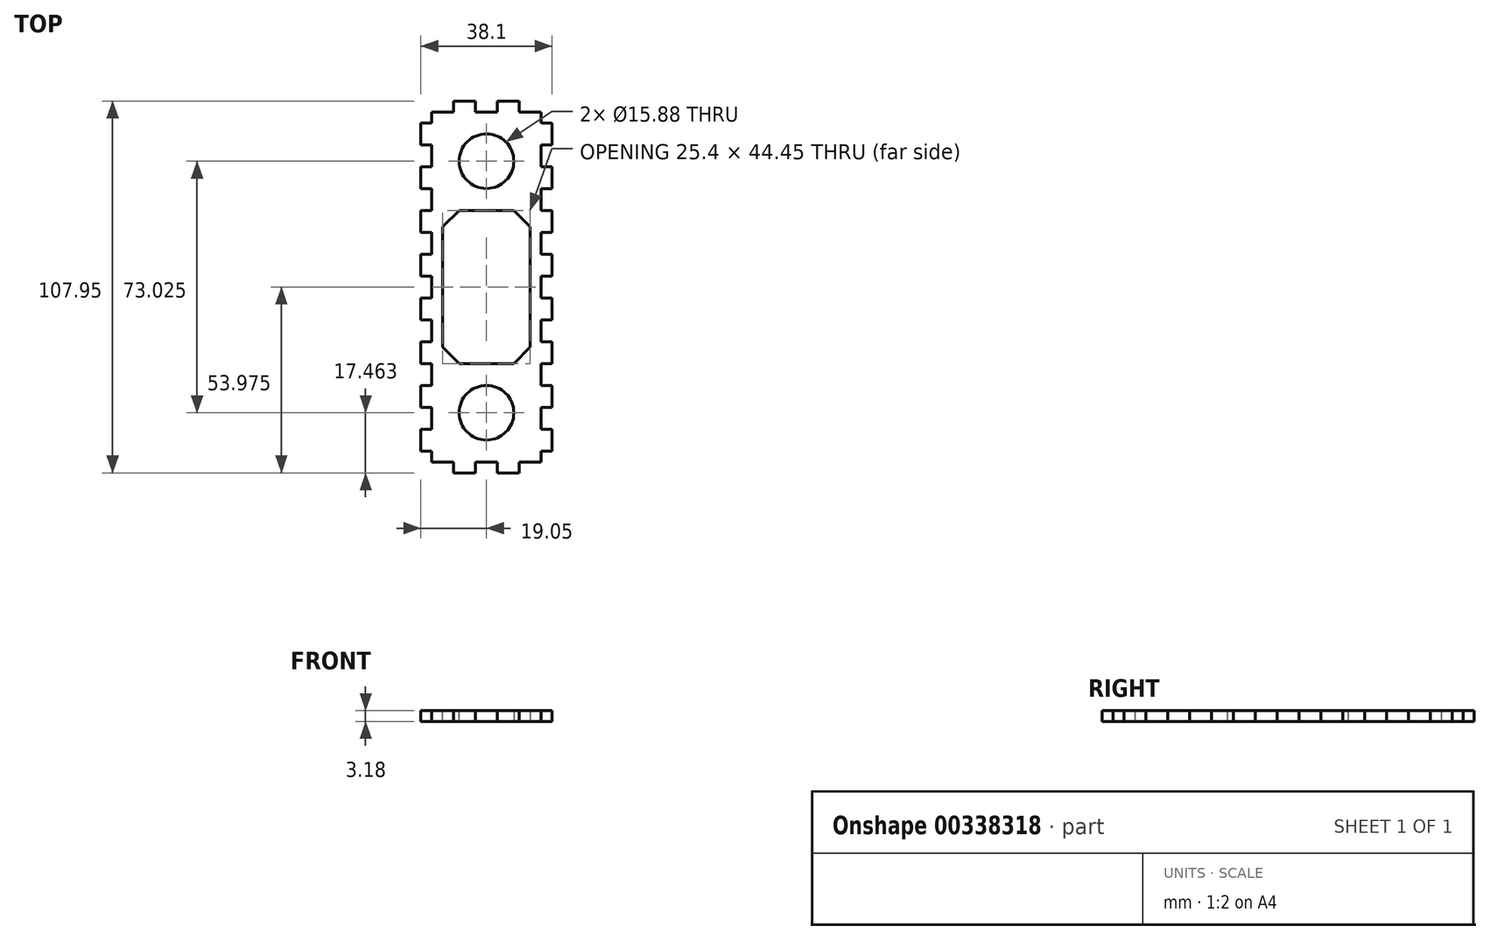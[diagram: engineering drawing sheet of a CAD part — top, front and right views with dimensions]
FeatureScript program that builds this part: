
annotation { "Feature Type Name" : "Feature", "Feature Type Description" : "" }
export const myFeature = defineFeature(function(context is Context, id is Id, definition is map)
    precondition{}
    {
        {
            var Q0;
            Q0=qCreatedBy(makeId("Top.planeOp"),FACE);
            var sketch = newSketch(context, id + "F0", { "sketchPlane" : qUnion([Q0])});
            skLineSegment(sketch, "E0.bottom", {"start": v(0, 0) * mm, "end": v(38.1, 0) * mm});
            skLineSegment(sketch, "E0.top", {"start": v(0, -107.95) * mm, "end": v(38.1, -107.95) * mm});
            skLineSegment(sketch, "E0.left", {"start": v(0, 0) * mm, "end": v(0, -107.95) * mm});
            skLineSegment(sketch, "E0.right", {"start": v(38.1, 0) * mm, "end": v(38.1, -107.95) * mm});
            skLineSegment(sketch, "E1", {"start": v(19.05, 0) * mm, "end": v(19.05, -17.46) * mm, "construction": true});
            skCircle(sketch, "E2", {"center": v(19.05, -17.46) * mm, "radius": 7.94 * mm});
            skLineSegment(sketch, "E3", {"start": v(19.05, -17.46) * mm, "end": v(19.05, -90.49) * mm, "construction": true});
            skLineSegment(sketch, "E4", {"start": v(19.05, -90.49) * mm, "end": v(19.05, -107.95) * mm, "construction": true});
            skCircle(sketch, "E5", {"center": v(19.05, -90.49) * mm, "radius": 7.94 * mm});
            skSolve(sketch);
        }
        {
            var Q0;
            Q0=qSketchRegion(id+"F0",true);
            extrude(context, id + "F1", {"entities" : qUnion([Q0]), "depth" : 3.17 * mm});
        }
        {
            var Q0;
            Q0=makeQuery(id+"F1.opExtrude","CAP_FACE",FACE,{"disambiguationData":[OSD([sQuery(id+"F0.wireOp",EDGE,"E0.bottom"),sQuery(id+"F0.wireOp",EDGE,"E0.top"),sQuery(id+"F0.wireOp",EDGE,"E0.left"),sQuery(id+"F0.wireOp",EDGE,"E0.right"),sQuery(id+"F0.wireOp",EDGE,"E2"),sQuery(id+"F0.wireOp",EDGE,"E5")])],"isStart":false});
            var sketch = newSketch(context, id + "F2", { "sketchPlane" : qUnion([Q0])});
            skLineSegment(sketch, "E6.bottom", {"start": v(38.1, 0) * mm, "end": v(34.93, 0) * mm});
            skLineSegment(sketch, "E6.top", {"start": v(38.1, -6.35) * mm, "end": v(34.93, -6.35) * mm});
            skLineSegment(sketch, "E6.left", {"start": v(38.1, 0) * mm, "end": v(38.1, -6.35) * mm});
            skLineSegment(sketch, "E6.right", {"start": v(34.93, 0) * mm, "end": v(34.93, -6.35) * mm});
            skLineSegment(sketch, "E7.bottom", {"start": v(0, 0) * mm, "end": v(3.17, 0) * mm});
            skLineSegment(sketch, "E7.top", {"start": v(0, -6.35) * mm, "end": v(3.17, -6.35) * mm});
            skLineSegment(sketch, "E7.left", {"start": v(0, 0) * mm, "end": v(0, -6.35) * mm});
            skLineSegment(sketch, "E7.right", {"start": v(3.17, 0) * mm, "end": v(3.17, -6.35) * mm});
            skLineSegment(sketch, "E8", {"start": v(3.17, -6.35) * mm, "end": v(3.17, -12.7) * mm, "construction": true});
            skLineSegment(sketch, "E9.bottom", {"start": v(3.17, -12.7) * mm, "end": v(0, -12.7) * mm});
            skLineSegment(sketch, "E9.top", {"start": v(3.17, -19.05) * mm, "end": v(0, -19.05) * mm});
            skLineSegment(sketch, "E9.left", {"start": v(3.17, -12.7) * mm, "end": v(3.17, -19.05) * mm});
            skLineSegment(sketch, "E9.right", {"start": v(0, -12.7) * mm, "end": v(0, -19.05) * mm});
            skLineSegment(sketch, "E10", {"start": v(34.93, -6.35) * mm, "end": v(34.93, -12.7) * mm, "construction": true});
            skLineSegment(sketch, "E11.bottom", {"start": v(34.93, -12.7) * mm, "end": v(38.1, -12.7) * mm});
            skLineSegment(sketch, "E11.top", {"start": v(34.93, -19.05) * mm, "end": v(38.1, -19.05) * mm});
            skLineSegment(sketch, "E11.left", {"start": v(34.93, -12.7) * mm, "end": v(34.93, -19.05) * mm});
            skLineSegment(sketch, "E11.right", {"start": v(38.1, -12.7) * mm, "end": v(38.1, -19.05) * mm});
            skLineSegment(sketch, "E12.0.1.0", {"start": v(34.93, -25.4) * mm, "end": v(38.1, -25.4) * mm});
            skLineSegment(sketch, "E12.0.1.1", {"start": v(34.93, -31.75) * mm, "end": v(38.1, -31.75) * mm});
            skLineSegment(sketch, "E12.0.1.2", {"start": v(34.93, -19.05) * mm, "end": v(34.93, -25.4) * mm, "construction": true});
            skLineSegment(sketch, "E12.0.1.3", {"start": v(38.1, -25.4) * mm, "end": v(38.1, -31.75) * mm});
            skLineSegment(sketch, "E12.0.1.4", {"start": v(34.93, -25.4) * mm, "end": v(34.93, -31.75) * mm});
            skLineSegment(sketch, "E12.0.2.0", {"start": v(34.93, -38.1) * mm, "end": v(38.1, -38.1) * mm});
            skLineSegment(sketch, "E12.0.2.1", {"start": v(34.93, -44.45) * mm, "end": v(38.1, -44.45) * mm});
            skLineSegment(sketch, "E12.0.2.2", {"start": v(34.93, -31.75) * mm, "end": v(34.93, -38.1) * mm, "construction": true});
            skLineSegment(sketch, "E12.0.2.3", {"start": v(38.1, -38.1) * mm, "end": v(38.1, -44.45) * mm});
            skLineSegment(sketch, "E12.0.2.4", {"start": v(34.93, -38.1) * mm, "end": v(34.93, -44.45) * mm});
            skLineSegment(sketch, "E12.0.3.0", {"start": v(34.93, -50.8) * mm, "end": v(38.1, -50.8) * mm});
            skLineSegment(sketch, "E12.0.3.1", {"start": v(34.93, -57.15) * mm, "end": v(38.1, -57.15) * mm});
            skLineSegment(sketch, "E12.0.3.2", {"start": v(34.93, -44.45) * mm, "end": v(34.93, -50.8) * mm, "construction": true});
            skLineSegment(sketch, "E12.0.3.3", {"start": v(38.1, -50.8) * mm, "end": v(38.1, -57.15) * mm});
            skLineSegment(sketch, "E12.0.3.4", {"start": v(34.93, -50.8) * mm, "end": v(34.93, -57.15) * mm});
            skLineSegment(sketch, "E12.0.4.0", {"start": v(34.93, -63.5) * mm, "end": v(38.1, -63.5) * mm});
            skLineSegment(sketch, "E12.0.4.1", {"start": v(34.93, -69.85) * mm, "end": v(38.1, -69.85) * mm});
            skLineSegment(sketch, "E12.0.4.2", {"start": v(34.93, -57.15) * mm, "end": v(34.93, -63.5) * mm, "construction": true});
            skLineSegment(sketch, "E12.0.4.3", {"start": v(38.1, -63.5) * mm, "end": v(38.1, -69.85) * mm});
            skLineSegment(sketch, "E12.0.4.4", {"start": v(34.93, -63.5) * mm, "end": v(34.93, -69.85) * mm});
            skLineSegment(sketch, "E12.0.5.0", {"start": v(34.93, -76.2) * mm, "end": v(38.1, -76.2) * mm});
            skLineSegment(sketch, "E12.0.5.1", {"start": v(34.93, -82.55) * mm, "end": v(38.1, -82.55) * mm});
            skLineSegment(sketch, "E12.0.5.2", {"start": v(34.93, -69.85) * mm, "end": v(34.93, -76.2) * mm, "construction": true});
            skLineSegment(sketch, "E12.0.5.3", {"start": v(38.1, -76.2) * mm, "end": v(38.1, -82.55) * mm});
            skLineSegment(sketch, "E12.0.5.4", {"start": v(34.93, -76.2) * mm, "end": v(34.93, -82.55) * mm});
            skLineSegment(sketch, "E12.0.6.0", {"start": v(34.93, -88.9) * mm, "end": v(38.1, -88.9) * mm});
            skLineSegment(sketch, "E12.0.6.1", {"start": v(34.93, -95.25) * mm, "end": v(38.1, -95.25) * mm});
            skLineSegment(sketch, "E12.0.6.2", {"start": v(34.93, -82.55) * mm, "end": v(34.93, -88.9) * mm, "construction": true});
            skLineSegment(sketch, "E12.0.6.3", {"start": v(38.1, -88.9) * mm, "end": v(38.1, -95.25) * mm});
            skLineSegment(sketch, "E12.0.6.4", {"start": v(34.93, -88.9) * mm, "end": v(34.93, -95.25) * mm});
            skLineSegment(sketch, "E12.0.7.0", {"start": v(34.93, -101.6) * mm, "end": v(38.1, -101.6) * mm});
            skLineSegment(sketch, "E12.0.7.1", {"start": v(34.93, -107.95) * mm, "end": v(38.1, -107.95) * mm});
            skLineSegment(sketch, "E12.0.7.2", {"start": v(34.93, -95.25) * mm, "end": v(34.93, -101.6) * mm, "construction": true});
            skLineSegment(sketch, "E12.0.7.3", {"start": v(38.1, -101.6) * mm, "end": v(38.1, -107.95) * mm});
            skLineSegment(sketch, "E12.0.7.4", {"start": v(34.93, -101.6) * mm, "end": v(34.93, -107.95) * mm});
            skLineSegment(sketch, "E12.0.8.0", {"start": v(34.93, -114.3) * mm, "end": v(38.1, -114.3) * mm});
            skLineSegment(sketch, "E12.0.8.1", {"start": v(34.93, -120.65) * mm, "end": v(38.1, -120.65) * mm});
            skLineSegment(sketch, "E12.0.8.2", {"start": v(34.93, -107.95) * mm, "end": v(34.93, -114.3) * mm, "construction": true});
            skLineSegment(sketch, "E12.0.8.3", {"start": v(38.1, -114.3) * mm, "end": v(38.1, -120.65) * mm});
            skLineSegment(sketch, "E12.0.8.4", {"start": v(34.93, -114.3) * mm, "end": v(34.93, -120.65) * mm});
            skLineSegment(sketch, "E12.0.9.0", {"start": v(34.93, -127) * mm, "end": v(38.1, -127) * mm});
            skLineSegment(sketch, "E12.0.9.1", {"start": v(34.93, -133.35) * mm, "end": v(38.1, -133.35) * mm});
            skLineSegment(sketch, "E12.0.9.2", {"start": v(34.93, -120.65) * mm, "end": v(34.93, -127) * mm, "construction": true});
            skLineSegment(sketch, "E12.0.9.3", {"start": v(38.1, -127) * mm, "end": v(38.1, -133.35) * mm});
            skLineSegment(sketch, "E12.0.9.4", {"start": v(34.93, -127) * mm, "end": v(34.93, -133.35) * mm});
            skLineSegment(sketch, "E12.direction1", {"start": v(17.46, -19.05) * mm, "end": v(34.93, -19.05) * mm, "construction": true});
            skLineSegment(sketch, "E12.direction2", {"start": v(34.93, -19.05) * mm, "end": v(34.93, -31.75) * mm, "construction": true});
            skLineSegment(sketch, "E13.0.1.0", {"start": v(3.17, -19.05) * mm, "end": v(3.17, -25.4) * mm, "construction": true});
            skLineSegment(sketch, "E13.0.1.1", {"start": v(3.17, -25.4) * mm, "end": v(0, -25.4) * mm});
            skLineSegment(sketch, "E13.0.1.2", {"start": v(3.17, -31.75) * mm, "end": v(0, -31.75) * mm});
            skLineSegment(sketch, "E13.0.1.3", {"start": v(3.17, -25.4) * mm, "end": v(3.17, -31.75) * mm});
            skLineSegment(sketch, "E13.0.1.4", {"start": v(0, -25.4) * mm, "end": v(0, -31.75) * mm});
            skLineSegment(sketch, "E13.0.2.0", {"start": v(3.17, -31.75) * mm, "end": v(3.17, -38.1) * mm, "construction": true});
            skLineSegment(sketch, "E13.0.2.1", {"start": v(3.17, -38.1) * mm, "end": v(0, -38.1) * mm});
            skLineSegment(sketch, "E13.0.2.2", {"start": v(3.17, -44.45) * mm, "end": v(0, -44.45) * mm});
            skLineSegment(sketch, "E13.0.2.3", {"start": v(3.17, -38.1) * mm, "end": v(3.17, -44.45) * mm});
            skLineSegment(sketch, "E13.0.2.4", {"start": v(0, -38.1) * mm, "end": v(0, -44.45) * mm});
            skLineSegment(sketch, "E13.0.3.0", {"start": v(3.17, -44.45) * mm, "end": v(3.17, -50.8) * mm, "construction": true});
            skLineSegment(sketch, "E13.0.3.1", {"start": v(3.17, -50.8) * mm, "end": v(0, -50.8) * mm});
            skLineSegment(sketch, "E13.0.3.2", {"start": v(3.17, -57.15) * mm, "end": v(0, -57.15) * mm});
            skLineSegment(sketch, "E13.0.3.3", {"start": v(3.17, -50.8) * mm, "end": v(3.17, -57.15) * mm});
            skLineSegment(sketch, "E13.0.3.4", {"start": v(0, -50.8) * mm, "end": v(0, -57.15) * mm});
            skLineSegment(sketch, "E13.0.4.0", {"start": v(3.17, -57.15) * mm, "end": v(3.17, -63.5) * mm, "construction": true});
            skLineSegment(sketch, "E13.0.4.1", {"start": v(3.17, -63.5) * mm, "end": v(0, -63.5) * mm});
            skLineSegment(sketch, "E13.0.4.2", {"start": v(3.17, -69.85) * mm, "end": v(0, -69.85) * mm});
            skLineSegment(sketch, "E13.0.4.3", {"start": v(3.17, -63.5) * mm, "end": v(3.17, -69.85) * mm});
            skLineSegment(sketch, "E13.0.4.4", {"start": v(0, -63.5) * mm, "end": v(0, -69.85) * mm});
            skLineSegment(sketch, "E13.0.5.0", {"start": v(3.17, -69.85) * mm, "end": v(3.17, -76.2) * mm, "construction": true});
            skLineSegment(sketch, "E13.0.5.1", {"start": v(3.17, -76.2) * mm, "end": v(0, -76.2) * mm});
            skLineSegment(sketch, "E13.0.5.2", {"start": v(3.17, -82.55) * mm, "end": v(0, -82.55) * mm});
            skLineSegment(sketch, "E13.0.5.3", {"start": v(3.17, -76.2) * mm, "end": v(3.17, -82.55) * mm});
            skLineSegment(sketch, "E13.0.5.4", {"start": v(0, -76.2) * mm, "end": v(0, -82.55) * mm});
            skLineSegment(sketch, "E13.0.6.0", {"start": v(3.17, -82.55) * mm, "end": v(3.17, -88.9) * mm, "construction": true});
            skLineSegment(sketch, "E13.0.6.1", {"start": v(3.17, -88.9) * mm, "end": v(0, -88.9) * mm});
            skLineSegment(sketch, "E13.0.6.2", {"start": v(3.17, -95.25) * mm, "end": v(0, -95.25) * mm});
            skLineSegment(sketch, "E13.0.6.3", {"start": v(3.17, -88.9) * mm, "end": v(3.17, -95.25) * mm});
            skLineSegment(sketch, "E13.0.6.4", {"start": v(0, -88.9) * mm, "end": v(0, -95.25) * mm});
            skLineSegment(sketch, "E13.0.7.0", {"start": v(3.17, -95.25) * mm, "end": v(3.17, -101.6) * mm, "construction": true});
            skLineSegment(sketch, "E13.0.7.1", {"start": v(3.17, -101.6) * mm, "end": v(0, -101.6) * mm});
            skLineSegment(sketch, "E13.0.7.2", {"start": v(3.17, -107.95) * mm, "end": v(0, -107.95) * mm});
            skLineSegment(sketch, "E13.0.7.3", {"start": v(3.17, -101.6) * mm, "end": v(3.17, -107.95) * mm});
            skLineSegment(sketch, "E13.0.7.4", {"start": v(0, -101.6) * mm, "end": v(0, -107.95) * mm});
            skLineSegment(sketch, "E13.0.8.0", {"start": v(3.17, -107.95) * mm, "end": v(3.17, -114.3) * mm, "construction": true});
            skLineSegment(sketch, "E13.0.8.1", {"start": v(3.17, -114.3) * mm, "end": v(0, -114.3) * mm});
            skLineSegment(sketch, "E13.0.8.2", {"start": v(3.17, -120.65) * mm, "end": v(0, -120.65) * mm});
            skLineSegment(sketch, "E13.0.8.3", {"start": v(3.17, -114.3) * mm, "end": v(3.17, -120.65) * mm});
            skLineSegment(sketch, "E13.0.8.4", {"start": v(0, -114.3) * mm, "end": v(0, -120.65) * mm});
            skLineSegment(sketch, "E13.0.9.0", {"start": v(3.17, -120.65) * mm, "end": v(3.17, -127) * mm, "construction": true});
            skLineSegment(sketch, "E13.0.9.1", {"start": v(3.17, -127) * mm, "end": v(0, -127) * mm});
            skLineSegment(sketch, "E13.0.9.2", {"start": v(3.17, -133.35) * mm, "end": v(0, -133.35) * mm});
            skLineSegment(sketch, "E13.0.9.3", {"start": v(3.17, -127) * mm, "end": v(3.17, -133.35) * mm});
            skLineSegment(sketch, "E13.0.9.4", {"start": v(0, -127) * mm, "end": v(0, -133.35) * mm});
            skLineSegment(sketch, "E13.direction1", {"start": v(0, -19.05) * mm, "end": v(17.46, -19.05) * mm, "construction": true});
            skLineSegment(sketch, "E13.direction2", {"start": v(0, -19.05) * mm, "end": v(0, -31.75) * mm, "construction": true});
            skLineSegment(sketch, "E14", {"start": v(19.05, 0) * mm, "end": v(19.05, -17.46) * mm, "construction": true});
            skLineSegment(sketch, "E15", {"start": v(19.05, -17.46) * mm, "end": v(19.05, -31.75) * mm, "construction": true});
            skLineSegment(sketch, "E16.bottom", {"start": v(6.35, -31.75) * mm, "end": v(31.75, -31.75) * mm});
            skLineSegment(sketch, "E16.top", {"start": v(6.35, -76.2) * mm, "end": v(31.75, -76.2) * mm});
            skLineSegment(sketch, "E16.left", {"start": v(6.35, -31.75) * mm, "end": v(6.35, -76.2) * mm});
            skLineSegment(sketch, "E16.right", {"start": v(31.75, -31.75) * mm, "end": v(31.75, -76.2) * mm});
            skLineSegment(sketch, "E17", {"start": v(31.75, -53.97) * mm, "end": v(34.93, -53.97) * mm, "construction": true});
            skPoint(sketch, "E18.oppositeSnap0", {"position": v(38.1, -3.18) * mm});
            skLineSegment(sketch, "E18.bottom", {"start": v(3.17, 0) * mm, "end": v(9.52, 0) * mm});
            skLineSegment(sketch, "E18.top", {"start": v(3.17, -3.17) * mm, "end": v(9.52, -3.17) * mm});
            skLineSegment(sketch, "E18.left", {"start": v(3.17, 0) * mm, "end": v(3.17, -3.18) * mm});
            skLineSegment(sketch, "E18.right", {"start": v(9.52, 0) * mm, "end": v(9.52, -3.18) * mm});
            skLineSegment(sketch, "E19.bottom", {"start": v(34.93, 0) * mm, "end": v(28.58, 0) * mm});
            skLineSegment(sketch, "E19.top", {"start": v(34.93, -3.17) * mm, "end": v(28.58, -3.17) * mm});
            skLineSegment(sketch, "E19.left", {"start": v(34.93, 0) * mm, "end": v(34.93, -3.18) * mm});
            skLineSegment(sketch, "E19.right", {"start": v(28.58, 0) * mm, "end": v(28.58, -3.18) * mm});
            skLineSegment(sketch, "E20.bottom", {"start": v(15.88, 0) * mm, "end": v(22.23, 0) * mm});
            skLineSegment(sketch, "E20.top", {"start": v(15.88, -3.17) * mm, "end": v(22.23, -3.17) * mm});
            skLineSegment(sketch, "E20.left", {"start": v(15.88, 0) * mm, "end": v(15.88, -3.18) * mm});
            skLineSegment(sketch, "E20.right", {"start": v(22.23, 0) * mm, "end": v(22.23, -3.18) * mm});
            skLineSegment(sketch, "E21", {"start": v(9.52, -3.18) * mm, "end": v(15.88, -3.17) * mm, "construction": true});
            skLineSegment(sketch, "E22", {"start": v(22.23, -3.17) * mm, "end": v(28.58, -3.17) * mm, "construction": true});
            skLineSegment(sketch, "E23", {"start": v(19.05, -90.49) * mm, "end": v(19.05, -107.95) * mm, "construction": true});
            skLineSegment(sketch, "E24.bottom", {"start": v(3.17, -107.95) * mm, "end": v(9.52, -107.95) * mm});
            skLineSegment(sketch, "E24.top", {"start": v(3.17, -104.78) * mm, "end": v(9.53, -104.78) * mm});
            skLineSegment(sketch, "E24.left", {"start": v(3.17, -107.95) * mm, "end": v(3.17, -104.78) * mm});
            skLineSegment(sketch, "E24.right", {"start": v(9.52, -107.95) * mm, "end": v(9.52, -104.78) * mm});
            skLineSegment(sketch, "E25.bottom", {"start": v(34.93, -107.95) * mm, "end": v(28.58, -107.95) * mm});
            skLineSegment(sketch, "E25.top", {"start": v(34.93, -104.78) * mm, "end": v(28.58, -104.78) * mm});
            skLineSegment(sketch, "E25.left", {"start": v(34.93, -107.95) * mm, "end": v(34.93, -104.78) * mm});
            skLineSegment(sketch, "E25.right", {"start": v(28.58, -107.95) * mm, "end": v(28.58, -104.78) * mm});
            skLineSegment(sketch, "E26.bottom", {"start": v(22.22, -107.95) * mm, "end": v(15.88, -107.95) * mm});
            skLineSegment(sketch, "E26.top", {"start": v(22.23, -104.78) * mm, "end": v(15.88, -104.78) * mm});
            skLineSegment(sketch, "E26.left", {"start": v(22.22, -107.95) * mm, "end": v(22.22, -104.78) * mm});
            skLineSegment(sketch, "E26.right", {"start": v(15.88, -107.95) * mm, "end": v(15.88, -104.78) * mm});
            skLineSegment(sketch, "E27", {"start": v(9.53, -104.78) * mm, "end": v(15.88, -104.78) * mm, "construction": true});
            skLineSegment(sketch, "E28", {"start": v(22.23, -104.78) * mm, "end": v(28.58, -104.78) * mm, "construction": true});
            skLineSegment(sketch, "E29", {"start": v(19.05, -90.49) * mm, "end": v(19.05, -76.2) * mm, "construction": true});
            skSolve(sketch);
        }
        {
            var Q0;
            Q0=qSketchRegion(id+"F2",true);
            var Q1;
            Q1=makeQuery(id+"F1.opExtrude","CAP_FACE",FACE,{"disambiguationData":[OSD([sQuery(id+"F0.wireOp",EDGE,"E0.bottom"),sQuery(id+"F0.wireOp",EDGE,"E0.top"),sQuery(id+"F0.wireOp",EDGE,"E0.left"),sQuery(id+"F0.wireOp",EDGE,"E0.right"),sQuery(id+"F0.wireOp",EDGE,"E2"),sQuery(id+"F0.wireOp",EDGE,"E5")])],"isStart":true});
            extrude(context, id + "F3", {"entities" : qUnion([Q0]), "operationType" : NewBodyOperationType.REMOVE, "endBound" : BoundingType.UP_TO_SURFACE, "oppositeDirection" : true, "endBoundEntityFace" : qUnion([Q1]), "depth" : 25.4 * mm});
        }
        {
            var Q0;
            Q0=makeQuery(id+"F3.boolean.opBoolean","COPY",EDGE,{"derivedFrom":makeQuery(id+"F3.opExtrude","SWEPT_EDGE",EDGE,{"disambiguationData":[OSD([sQuery(id+"F2.wireOp",EDGE,"E16.bottom"),sQuery(id+"F2.wireOp",EDGE,"E16.right")])]})});
            var Q1;
            Q1=makeQuery(id+"F3.boolean.opBoolean","COPY",EDGE,{"derivedFrom":makeQuery(id+"F3.opExtrude","SWEPT_EDGE",EDGE,{"disambiguationData":[OSD([sQuery(id+"F2.wireOp",EDGE,"E16.top"),sQuery(id+"F2.wireOp",EDGE,"E16.right")])]})});
            var Q2;
            Q2=makeQuery(id+"F3.boolean.opBoolean","COPY",EDGE,{"derivedFrom":makeQuery(id+"F3.opExtrude","SWEPT_EDGE",EDGE,{"disambiguationData":[OSD([sQuery(id+"F2.wireOp",EDGE,"E16.top"),sQuery(id+"F2.wireOp",EDGE,"E16.left")])]})});
            var Q3;
            Q3=makeQuery(id+"F3.boolean.opBoolean","COPY",EDGE,{"derivedFrom":makeQuery(id+"F3.opExtrude","SWEPT_EDGE",EDGE,{"disambiguationData":[OSD([sQuery(id+"F2.wireOp",EDGE,"E16.bottom"),sQuery(id+"F2.wireOp",EDGE,"E16.left")])]})});
            chamfer(context, id + "F4", {"entities" : qUnion([Q0, Q1, Q2, Q3]), "width" : 4.76 * mm, "tangentPropagation" : true});
        }
    });
